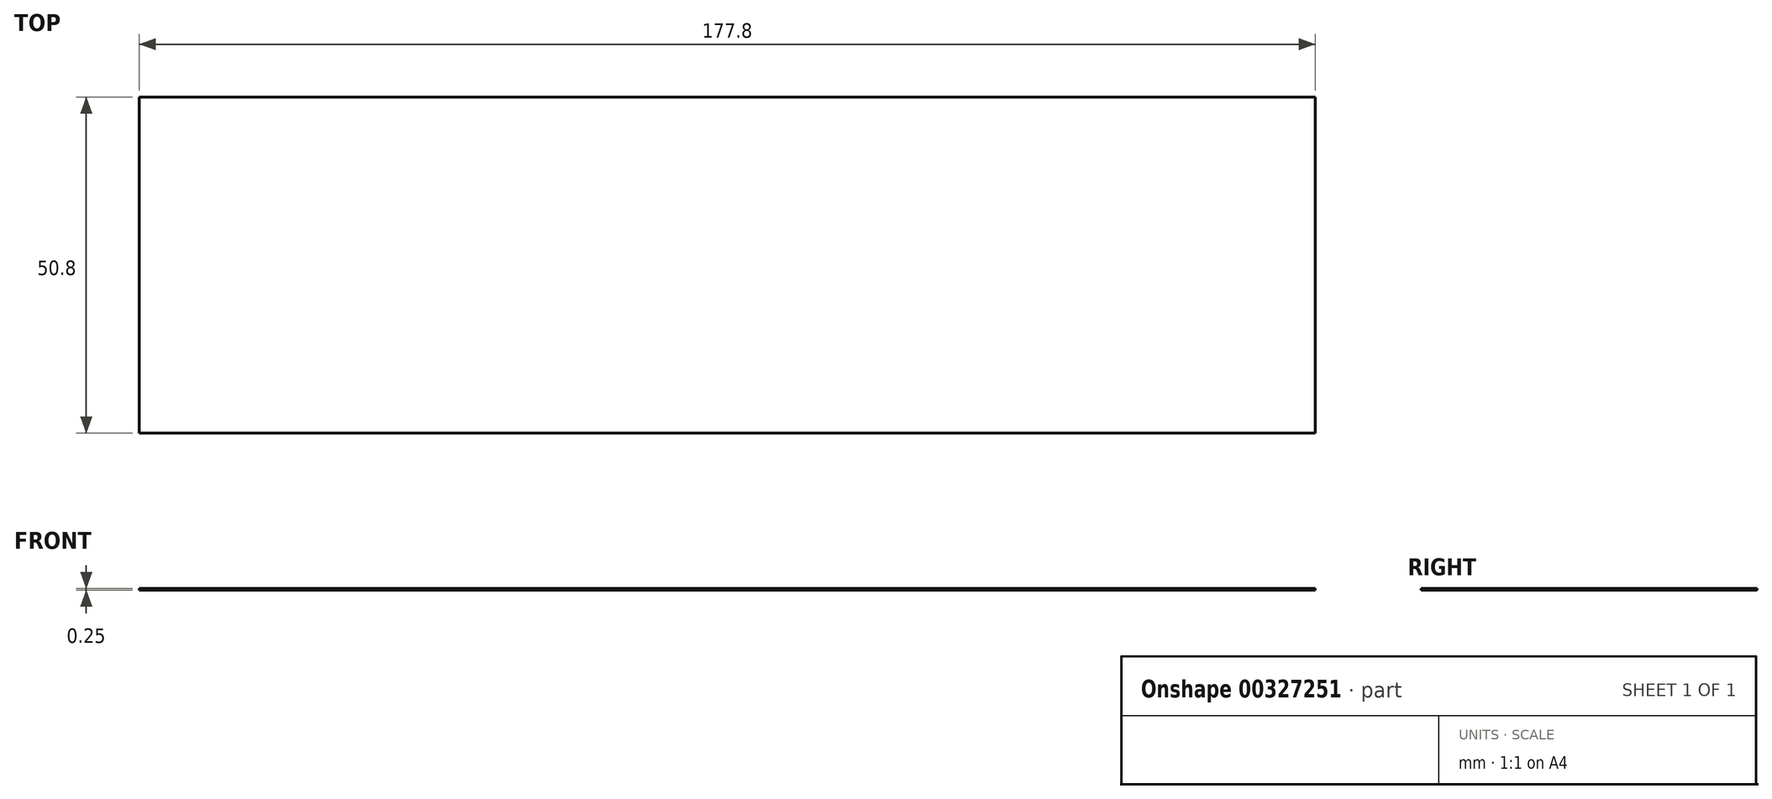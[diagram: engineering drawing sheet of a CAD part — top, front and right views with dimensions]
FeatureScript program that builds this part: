
annotation { "Feature Type Name" : "Feature", "Feature Type Description" : "" }
export const myFeature = defineFeature(function(context is Context, id is Id, definition is map)
    precondition{}
    {
        {
            assignVariable(context, id + "F0", {"name" : "THKNS", "anyValue" : .25});
        }
        {
            var Q0;
            Q0=qCreatedBy(makeId("Top.planeOp"),FACE);
            var sketch = newSketch(context, id + "F1", { "sketchPlane" : qUnion([Q0])});
            skLineSegment(sketch, "E0.bottom", {"start": v(0, 50.8) * mm, "end": v(177.8, 50.8) * mm});
            skLineSegment(sketch, "E0.top", {"start": v(0, 0) * mm, "end": v(177.8, 0) * mm});
            skLineSegment(sketch, "E0.left", {"start": v(0, 50.8) * mm, "end": v(0, 0) * mm});
            skLineSegment(sketch, "E0.right", {"start": v(177.8, 50.8) * mm, "end": v(177.8, 0) * mm});
            skSolve(sketch);
        }
        {
            var Q0;
            Q0=qSketchRegion(id+"F1",true);
            extrude(context, id + "F2", {"entities" : qUnion([Q0]), "depth" : (getVariable(context, 'THKNS')) * mm});
        }
    });
